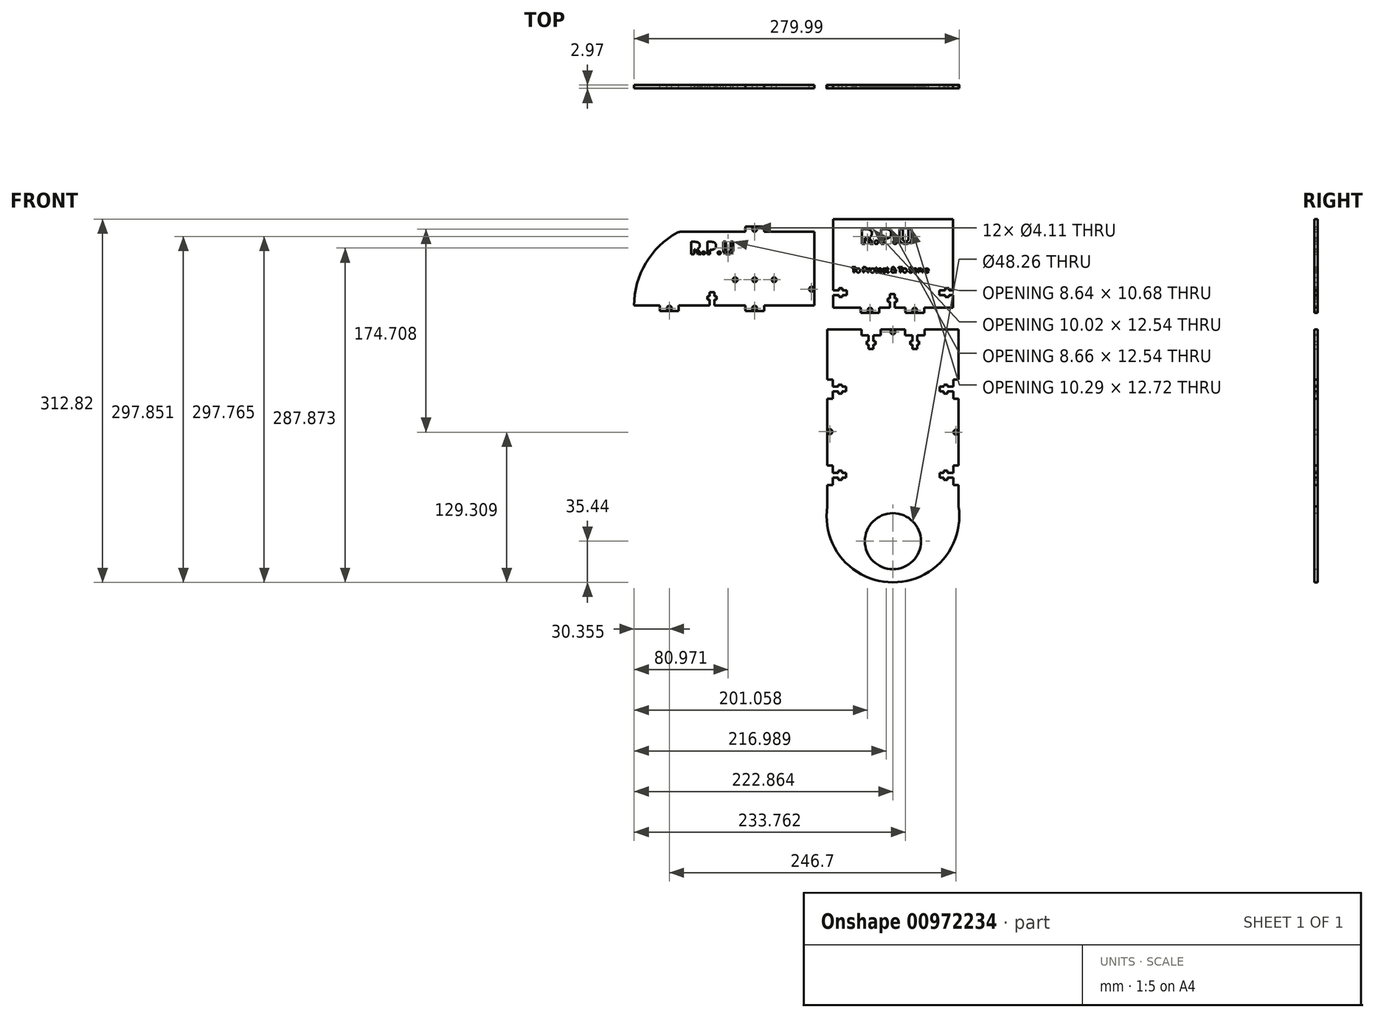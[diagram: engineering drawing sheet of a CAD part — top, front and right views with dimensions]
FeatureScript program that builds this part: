
annotation { "Feature Type Name" : "Feature", "Feature Type Description" : "" }
export const myFeature = defineFeature(function(context is Context, id is Id, definition is map)
    precondition{}
    {
        {
            var Q0;
            Q0=qCreatedBy(makeId("Front.planeOp"),FACE);
            var sketch = newSketch(context, id + "F0", { "sketchPlane" : qUnion([Q0])});
            skCircle(sketch, "E0", {"center": v(-10.51, -12.98) * mm, "radius": 2.06 * mm});
            skLineSegment(sketch, "E1.top", {"start": v(-18.6, -15.29) * mm, "end": v(-2.43, -15.29) * mm});
            skCircle(sketch, "E2", {"center": v(27.94, -12.98) * mm, "radius": 2.06 * mm});
            skLineSegment(sketch, "E3", {"start": v(19.85, -15.29) * mm, "end": v(36.02, -15.29) * mm});
            skLineSegment(sketch, "E4", {"start": v(-38.26, -10.74) * mm, "end": v(-18.6, -10.74) * mm});
            skLineSegment(sketch, "E5", {"start": v(-2.43, -15.29) * mm, "end": v(-2.43, -10.74) * mm});
            skLineSegment(sketch, "E6", {"start": v(-18.6, -15.29) * mm, "end": v(-18.6, -10.74) * mm});
            skLineSegment(sketch, "E7", {"start": v(36.02, -15.29) * mm, "end": v(36.02, -10.74) * mm});
            skLineSegment(sketch, "E8", {"start": v(19.85, -15.29) * mm, "end": v(19.85, -10.74) * mm});
            skLineSegment(sketch, "E9.trimOffspring", {"start": v(-2.43, -10.74) * mm, "end": v(6.65, -10.74) * mm});
            skLineSegment(sketch, "E10.trimOffspring", {"start": v(36.02, -10.74) * mm, "end": v(58.06, -10.74) * mm});
            skLineSegment(sketch, "E11", {"start": v(-38.26, -10.74) * mm, "end": v(-42.22, -10.74) * mm});
            skLineSegment(sketch, "E12", {"start": v(58.06, -10.74) * mm, "end": v(61.06, -10.74) * mm});
            skLineSegment(sketch, "E13", {"start": v(-42.22, 10.39) * mm, "end": v(-42.22, 4.11) * mm});
            skLineSegment(sketch, "E14", {"start": v(61.06, 10.39) * mm, "end": v(61.06, 4.11) * mm});
            skLineSegment(sketch, "E15", {"start": v(61.06, 0) * mm, "end": v(57.32, 0) * mm});
            skLineSegment(sketch, "E16.trimOffspring", {"start": v(61.06, 0) * mm, "end": v(61.06, -6.27) * mm});
            skLineSegment(sketch, "E17", {"start": v(-42.22, 0) * mm, "end": v(-37.14, 0) * mm});
            skLineSegment(sketch, "E18.trimOffspring", {"start": v(-42.22, 0) * mm, "end": v(-42.22, -6.27) * mm});
            skLineSegment(sketch, "E19", {"start": v(6.65, -10.74) * mm, "end": v(6.65, -5.66) * mm});
            skLineSegment(sketch, "E20.trimOffspring", {"start": v(10.77, -10.74) * mm, "end": v(19.85, -10.74) * mm});
            skLineSegment(sketch, "E21", {"start": v(-42.22, 65.46) * mm, "end": v(61.06, 65.46) * mm});
            skLineSegment(sketch, "E22.trimOffspring", {"start": v(-30.47, 4.11) * mm, "end": v(-34.21, 4.11) * mm});
            skLineSegment(sketch, "E23.trimOffspring", {"start": v(49.32, 4.11) * mm, "end": v(54.4, 4.11) * mm});
            skLineSegment(sketch, "E24.trimOffspring", {"start": v(10.77, 1) * mm, "end": v(10.77, -2.74) * mm});
            skText(sketch, "E25", { "text": "To Protect & To Serve", "fontName": "OpenSans-Bold.ttf"});
            skLineSegment(sketch, "E26", {"start": v(49.32, 4.11) * mm, "end": v(49.32, 0) * mm});
            skPoint(sketch, "E27.startSnap0", {"position": v(49.32, -3.14) * mm});
            skPoint(sketch, "E28.end.orphan", {"position": v(49.32, 10.39) * mm});
            skPoint(sketch, "E29.end.orphan", {"position": v(43.4, 10.39) * mm});
            skPoint(sketch, "E30.end.orphan", {"position": v(43.4, 4.11) * mm});
            skPoint(sketch, "E31.end.orphan", {"position": v(37.56, 4.11) * mm});
            skPoint(sketch, "E32.trimOffspring.end.orphan", {"position": v(37.56, 0) * mm});
            skPoint(sketch, "E33.end.orphan", {"position": v(43.4, 0) * mm});
            skPoint(sketch, "E34.end.orphan", {"position": v(43.4, -6.27) * mm});
            skPoint(sketch, "E35.orphan", {"position": v(49.32, -6.27) * mm});
            skLineSegment(sketch, "E36", {"start": v(54.4, -1.78) * mm, "end": v(57.32, -1.78) * mm});
            skLineSegment(sketch, "E37", {"start": v(57.32, -1.78) * mm, "end": v(57.32, 0) * mm});
            skLineSegment(sketch, "E38", {"start": v(54.4, 4.11) * mm, "end": v(54.4, 5.9) * mm});
            skLineSegment(sketch, "E39", {"start": v(54.4, 5.9) * mm, "end": v(57.3, 5.9) * mm});
            skLineSegment(sketch, "E40", {"start": v(57.3, 5.9) * mm, "end": v(57.3, 4.11) * mm});
            skLineSegment(sketch, "E41.trimOffspring", {"start": v(57.3, 4.11) * mm, "end": v(61.06, 4.11) * mm});
            skLineSegment(sketch, "E42", {"start": v(54.4, 0) * mm, "end": v(54.4, -1.78) * mm});
            skLineSegment(sketch, "E43.trimOffspring", {"start": v(54.4, 0) * mm, "end": v(49.32, 0) * mm});
            skLineSegment(sketch, "E44", {"start": v(-30.47, 4.11) * mm, "end": v(-30.47, 0) * mm});
            skLineSegment(sketch, "E45", {"start": v(6.65, 1) * mm, "end": v(10.77, 1) * mm});
            skLineSegment(sketch, "E46", {"start": v(61.06, -6.27) * mm, "end": v(61.06, -10.74) * mm});
            skPoint(sketch, "E47.orphan", {"position": v(65.6, -10.74) * mm});
            skPoint(sketch, "E48.start.orphan", {"position": v(65.6, -6.27) * mm});
            skLineSegment(sketch, "E49", {"start": v(-42.22, -6.27) * mm, "end": v(-42.22, -10.74) * mm});
            skPoint(sketch, "E50.orphan", {"position": v(-46.77, -10.74) * mm});
            skLineSegment(sketch, "E51", {"start": v(-37.14, 4.11) * mm, "end": v(-37.14, 5.9) * mm});
            skLineSegment(sketch, "E52", {"start": v(-37.14, 5.9) * mm, "end": v(-34.21, 5.9) * mm});
            skLineSegment(sketch, "E53", {"start": v(-34.21, 5.9) * mm, "end": v(-34.21, 4.11) * mm});
            skLineSegment(sketch, "E54.trimOffspring", {"start": v(-37.14, 4.11) * mm, "end": v(-42.22, 4.11) * mm});
            skLineSegment(sketch, "E55.trimOffspring", {"start": v(-34.21, 0) * mm, "end": v(-30.47, 0) * mm});
            skLineSegment(sketch, "E56", {"start": v(-37.14, 0) * mm, "end": v(-37.14, -1.75) * mm});
            skLineSegment(sketch, "E57", {"start": v(-37.14, -1.75) * mm, "end": v(-34.21, -1.75) * mm});
            skLineSegment(sketch, "E58", {"start": v(-34.21, -1.75) * mm, "end": v(-34.21, 0) * mm});
            skLineSegment(sketch, "E59", {"start": v(4.88, -5.66) * mm, "end": v(6.65, -5.66) * mm});
            skLineSegment(sketch, "E60", {"start": v(4.88, -5.66) * mm, "end": v(4.88, -2.74) * mm});
            skLineSegment(sketch, "E61", {"start": v(4.88, -2.74) * mm, "end": v(6.65, -2.74) * mm});
            skLineSegment(sketch, "E62", {"start": v(10.77, -5.66) * mm, "end": v(12.55, -5.66) * mm});
            skLineSegment(sketch, "E63", {"start": v(12.55, -5.66) * mm, "end": v(12.55, -2.74) * mm});
            skLineSegment(sketch, "E64", {"start": v(12.55, -2.74) * mm, "end": v(10.77, -2.74) * mm});
            skLineSegment(sketch, "E65.trimOffspring", {"start": v(10.77, -5.66) * mm, "end": v(10.77, -10.74) * mm});
            skLineSegment(sketch, "E66.trimOffspring", {"start": v(6.65, -2.74) * mm, "end": v(6.65, 1) * mm});
            skText(sketch, "E67", { "text": "R.P.U", "fontName": "OpenSans-Bold.ttf"});
            skLineSegment(sketch, "E68", {"start": v(-42.22, 10.39) * mm, "end": v(-42.22, 65.46) * mm});
            skPoint(sketch, "E69.orphan", {"position": v(-46.77, 65.46) * mm});
            skPoint(sketch, "E70.start.orphan", {"position": v(-46.77, 14.3) * mm});
            skLineSegment(sketch, "E71", {"start": v(61.06, 10.39) * mm, "end": v(61.06, 65.46) * mm});
            skPoint(sketch, "E72.end.orphan", {"position": v(65.6, 10.39) * mm});
            skPoint(sketch, "E72.start.orphan", {"position": v(65.6, 14.43) * mm});
            skPoint(sketch, "E73.orphan", {"position": v(65.6, 65.46) * mm});
            const initialGuessF0  = {"E25": [-0.02625, 0.0195, 1, 0, 0.00451], "E67": [-0.0192, 0.04422, 1, 0, 0.01265]};
            skSetInitialGuess(sketch, initialGuessF0);
            skSolve(sketch);
        }
        {
            var Q0;
            Q0=makeQuery(id+"F0.imprint","IMPRINT",FACE,{"disambiguationData":[TD([[makeQuery(id+"F0.imprint","IMPRINT",EDGE,{"derivedFrom":sQuery(id+"F0.wireOp",EDGE,"E0")}),-1.0]])]});
            extrude(context, id + "F1", {"entities" : qUnion([Q0]), "depth" : 2.97 * mm, "offsetDistance" : 25.4 * mm});
        }
        {
            var Q0;
            Q0=qCreatedBy(makeId("Front.planeOp"),FACE);
            var sketch = newSketch(context, id + "F2", { "sketchPlane" : qUnion([Q0])});
            skLineSegment(sketch, "E74", {"start": v(-36, -9.08) * mm, "end": v(-36, -2.95) * mm});
            skLineSegment(sketch, "E75", {"start": v(-36, -9.08) * mm, "end": v(-79.18, -9.08) * mm});
            skLineSegment(sketch, "E76", {"start": v(-79.18, -13.62) * mm, "end": v(-79.18, -9.08) * mm});
            skLineSegment(sketch, "E77", {"start": v(-79.18, -13.62) * mm, "end": v(-95.33, -13.62) * mm});
            skLineSegment(sketch, "E78", {"start": v(-95.33, -13.62) * mm, "end": v(-95.33, -9.08) * mm});
            skCircle(sketch, "E79", {"center": v(-87.25, -11.31) * mm, "radius": 2.06 * mm});
            skPoint(sketch, "E79.centerSnap0", {"position": v(-87.25, -13.62) * mm});
            skLineSegment(sketch, "E80.trimOffspring", {"start": v(-132.31, -9.08) * mm, "end": v(-152.63, -9.08) * mm});
            skLineSegment(sketch, "E81", {"start": v(-152.63, -13.62) * mm, "end": v(-152.63, -9.08) * mm});
            skLineSegment(sketch, "E82", {"start": v(-152.63, -13.62) * mm, "end": v(-168.79, -13.62) * mm});
            skLineSegment(sketch, "E83", {"start": v(-168.79, -13.62) * mm, "end": v(-168.79, -9.08) * mm});
            skCircle(sketch, "E84", {"center": v(-160.7, -11.31) * mm, "radius": 2.06 * mm});
            skPoint(sketch, "E84.centerSnap0", {"position": v(-160.7, -13.62) * mm});
            skLineSegment(sketch, "E85", {"start": v(-36, 54.42) * mm, "end": v(-79.18, 54.42) * mm});
            skLineSegment(sketch, "E86.trimOffspring", {"start": v(-95.33, -9.08) * mm, "end": v(-115.65, -9.08) * mm});
            skLineSegment(sketch, "E87.trimOffspring", {"start": v(-36, 13.2) * mm, "end": v(-36, 54.42) * mm});
            skLineSegment(sketch, "E88", {"start": v(-191.06, -9.08) * mm, "end": v(-168.79, -9.08) * mm});
            skLineSegment(sketch, "E89.trimOffspring", {"start": v(-168.79, 54.42) * mm, "end": v(-191.06, 54.42) * mm});
            skPoint(sketch, "E90", {"position": v(-87.25, 13.2) * mm});
            skCircle(sketch, "E91", {"center": v(-87.25, 13.2) * mm, "radius": 2.06 * mm});
            skCircle(sketch, "E92", {"center": v(-104.02, 13.2) * mm, "radius": 2.06 * mm});
            skCircle(sketch, "E93", {"center": v(-70.49, 13.2) * mm, "radius": 2.06 * mm});
            skText(sketch, "E94", { "text": "R.P.U\n", "fontName": "OpenSans-Bold.ttf"});
            skLineSegment(sketch, "E95", {"start": v(-191.06, 54.42) * mm, "end": v(-191.06, -9.08) * mm});
            skLineSegment(sketch, "E96", {"start": v(-168.79, 54.42) * mm, "end": v(-152.63, 54.42) * mm});
            skLineSegment(sketch, "E97", {"start": v(-95.33, 54.42) * mm, "end": v(-95.33, 58.97) * mm});
            skLineSegment(sketch, "E98", {"start": v(-95.33, 58.97) * mm, "end": v(-79.18, 58.97) * mm});
            skLineSegment(sketch, "E99", {"start": v(-79.18, 58.97) * mm, "end": v(-79.18, 54.42) * mm});
            skCircle(sketch, "E100", {"center": v(-87.25, 56.66) * mm, "radius": 2.06 * mm});
            skPoint(sketch, "E100.centerSnap0", {"position": v(-87.25, 58.97) * mm});
            skLineSegment(sketch, "E101.trimOffspring", {"start": v(-95.33, 54.42) * mm, "end": v(-152.63, 54.42) * mm});
            skArc(sketch, "E102", {"start": v(-152.63, 54.42) * mm, "mid": v(-180.7, 28.03) * mm, "end": v(-191.06, -9.08) * mm});
            skLineSegment(sketch, "E103", {"start": v(-36, 13.2) * mm, "end": v(-40.54, 13.2) * mm});
            skLineSegment(sketch, "E104", {"start": v(-36, -2.95) * mm, "end": v(-40.54, -2.95) * mm});
            skCircle(sketch, "E105", {"center": v(-38.3, 5.12) * mm, "radius": 2.06 * mm});
            skPoint(sketch, "E105.centerSnap0", {"position": v(-40.54, 5.12) * mm});
            skLineSegment(sketch, "E106", {"start": v(-36, 13.2) * mm, "end": v(-36, -2.95) * mm});
            skLineSegment(sketch, "E107", {"start": v(-132.31, -9.08) * mm, "end": v(-126.04, -9.08) * mm});
            skLineSegment(sketch, "E108", {"start": v(-115.65, -9.08) * mm, "end": v(-121.92, -9.08) * mm});
            skLineSegment(sketch, "E109", {"start": v(-121.92, -9.08) * mm, "end": v(-121.92, -4) * mm});
            skLineSegment(sketch, "E110", {"start": v(-126.04, -9.08) * mm, "end": v(-126.04, -4) * mm});
            skLineSegment(sketch, "E111", {"start": v(-126.04, -4) * mm, "end": v(-127.82, -4) * mm});
            skLineSegment(sketch, "E112", {"start": v(-127.82, -4) * mm, "end": v(-127.82, -1.08) * mm});
            skLineSegment(sketch, "E113", {"start": v(-127.82, -1.08) * mm, "end": v(-126.04, -1.08) * mm});
            skLineSegment(sketch, "E114", {"start": v(-121.92, -4) * mm, "end": v(-120.15, -4) * mm});
            skLineSegment(sketch, "E115", {"start": v(-120.15, -4) * mm, "end": v(-120.15, -1.08) * mm});
            skLineSegment(sketch, "E116", {"start": v(-120.15, -1.08) * mm, "end": v(-121.92, -1.08) * mm});
            skLineSegment(sketch, "E117", {"start": v(-121.92, -1.08) * mm, "end": v(-121.92, 2.66) * mm});
            skLineSegment(sketch, "E118", {"start": v(-126.04, -1.08) * mm, "end": v(-126.04, 2.66) * mm});
            skLineSegment(sketch, "E119", {"start": v(-126.04, 2.66) * mm, "end": v(-121.92, 2.66) * mm});
            const initialGuessF2  = {"E94": [-0.14308, 0.03532, 1, 0, 0.01062]};
            skSetInitialGuess(sketch, initialGuessF2);
            skSolve(sketch);
        }
        {
            var Q0;
            {var subQ1=sQuery(id+"F2.wireOp",EDGE,"OVJFDN25-UqmM-4DHd-mgfS-xPrGIr8piSGO");Q0=makeQuery(id+"F2.imprint","IMPRINT",FACE,{"disambiguationData":[TD([[makeQuery(id+"F2.imprint","IMPRINT",EDGE,{"derivedFrom":subQ1}),-1.0]])]});}
            var Q1;
            {var subQ2=sQuery(id+"F2.wireOp",EDGE,"OVJFDN25-UqmM-4DHd-mgfS-xPrGIr8piSGO");Q1=makeQuery(id+"F2.imprint","IMPRINT",FACE,{"disambiguationData":[TD([[makeQuery(id+"F2.imprint","IMPRINT",EDGE,{"derivedFrom":subQ2}),1.0]])]});}
            var Q2;
            {var subQ1=sQuery(id+"F2.wireOp",EDGE,"E76");Q2=makeQuery(id+"F2.imprint","IMPRINT",FACE,{"disambiguationData":[TD([[makeQuery(id+"F2.imprint","IMPRINT",EDGE,{"derivedFrom":subQ1}),1.0]])]});}
            extrude(context, id + "F3", {"entities" : qUnion([Q0, Q1, Q2]), "depth" : 2.97 * mm, "offsetDistance" : 25.4 * mm});
        }
        {
            var Q0;
            Q0=qCreatedBy(makeId("Front.planeOp"),FACE);
            var sketch = newSketch(context, id + "F4", { "sketchPlane" : qUnion([Q0])});
            skLineSegment(sketch, "E120", {"start": v(-47.3, -38.57) * mm, "end": v(-17.97, -38.57) * mm});
            skLineSegment(sketch, "E121", {"start": v(65.7, -38.57) * mm, "end": v(65.7, -81.75) * mm});
            skLineSegment(sketch, "E122", {"start": v(-47.3, -38.57) * mm, "end": v(-47.3, -81.75) * mm});
            skLineSegment(sketch, "E123", {"start": v(-47.3, -190.97) * mm, "end": v(65.7, -190.97) * mm});
            skLineSegment(sketch, "E124", {"start": v(65.7, -38.57) * mm, "end": v(36.36, -38.57) * mm});
            skLineSegment(sketch, "E125.trimOffspring", {"start": v(-1.3, -38.57) * mm, "end": v(19.7, -38.57) * mm});
            skCircle(sketch, "E126", {"center": v(9.2, -40.88) * mm, "radius": 2.06 * mm});
            skLineSegment(sketch, "E127", {"start": v(-17.97, -43.64) * mm, "end": v(-17.97, -38.57) * mm});
            skLineSegment(sketch, "E128", {"start": v(-17.97, -43.64) * mm, "end": v(-11.7, -43.64) * mm});
            skPoint(sketch, "E129.end.orphan", {"position": v(-8.78, -55.39) * mm});
            skLineSegment(sketch, "E130", {"start": v(-47.3, -81.75) * mm, "end": v(-42.74, -81.75) * mm});
            skLineSegment(sketch, "E131", {"start": v(-42.74, -98.41) * mm, "end": v(-47.3, -98.41) * mm});
            skLineSegment(sketch, "E132.trimOffspring", {"start": v(-47.3, -98.41) * mm, "end": v(-47.3, -119.12) * mm});
            skLineSegment(sketch, "E133", {"start": v(-42.74, -81.75) * mm, "end": v(-42.74, -88.02) * mm});
            skLineSegment(sketch, "E134", {"start": v(-42.74, -98.41) * mm, "end": v(-42.74, -92.14) * mm});
            skPoint(sketch, "E135.start.orphan", {"position": v(-42.74, -38.57) * mm});
            skPoint(sketch, "E136.start.orphan", {"position": v(-42.74, -118.73) * mm});
            skLineSegment(sketch, "E137.trimOffspring", {"start": v(-47.3, -135.27) * mm, "end": v(-47.3, -155.97) * mm});
            skLineSegment(sketch, "E138", {"start": v(-47.3, -155.97) * mm, "end": v(-42.74, -155.97) * mm});
            skLineSegment(sketch, "E139", {"start": v(-42.74, -172.63) * mm, "end": v(-47.3, -172.63) * mm});
            skLineSegment(sketch, "E140.trimOffspring", {"start": v(-47.3, -172.63) * mm, "end": v(-47.3, -190.97) * mm});
            skLineSegment(sketch, "E141", {"start": v(-42.74, -172.63) * mm, "end": v(-42.74, -166.36) * mm});
            skLineSegment(sketch, "E142", {"start": v(-42.74, -155.97) * mm, "end": v(-42.74, -162.24) * mm});
            skLineSegment(sketch, "E143", {"start": v(-42.74, -162.24) * mm, "end": v(-37.66, -162.24) * mm});
            skLineSegment(sketch, "E144", {"start": v(-42.74, -166.36) * mm, "end": v(-37.66, -166.36) * mm});
            skLineSegment(sketch, "E145", {"start": v(-42.74, -88.02) * mm, "end": v(-37.66, -88.02) * mm});
            skLineSegment(sketch, "E146", {"start": v(-42.74, -92.14) * mm, "end": v(-37.66, -92.14) * mm});
            skLineSegment(sketch, "E147", {"start": v(9.2, -40.88) * mm, "end": v(7.57, -38.57) * mm});
            skLineSegment(sketch, "E148", {"start": v(9.2, -40.88) * mm, "end": v(9.2, -190.97) * mm, "construction": true});
            skLineSegment(sketch, "E149.MirrorCS", {"start": v(65.7, -135.27) * mm, "end": v(65.7, -155.97) * mm});
            skLineSegment(sketch, "E150.MirrorCS", {"start": v(65.7, -172.63) * mm, "end": v(65.7, -190.97) * mm});
            skLineSegment(sketch, "E151.MirrorCS", {"start": v(65.7, -98.41) * mm, "end": v(65.7, -119.12) * mm});
            skPoint(sketch, "E152.MirrorP", {"position": v(61.12, -118.73) * mm});
            skLineSegment(sketch, "E153", {"start": v(-31, -92.14) * mm, "end": v(-31, -88.02) * mm});
            skLineSegment(sketch, "E154", {"start": v(-31, -162.24) * mm, "end": v(-31, -166.36) * mm});
            skPoint(sketch, "E155.start.orphan", {"position": v(-31, -155.6) * mm});
            skPoint(sketch, "E156.start.orphan", {"position": v(-31, -173.01) * mm});
            skPoint(sketch, "E157.end.orphan", {"position": v(-31, -98.03) * mm});
            skPoint(sketch, "E158.start.orphan", {"position": v(-25.08, -98.03) * mm});
            skPoint(sketch, "E159.start.orphan", {"position": v(-25.08, -92.14) * mm});
            skPoint(sketch, "E160.end.orphan", {"position": v(-19.24, -88.02) * mm});
            skPoint(sketch, "E160.start.orphan", {"position": v(-19.24, -91.37) * mm});
            skPoint(sketch, "E161.start.orphan", {"position": v(-31, -81.37) * mm});
            skPoint(sketch, "E162.end.orphan", {"position": v(-25.08, -88.02) * mm});
            skPoint(sketch, "E162.start.orphan", {"position": v(-25.08, -81.37) * mm});
            skPoint(sketch, "E163.end.orphan", {"position": v(-1.3, -61.3) * mm});
            skPoint(sketch, "E164.end.orphan", {"position": v(-4.55, -55.37) * mm});
            skPoint(sketch, "E165.end.orphan", {"position": v(-17.97, -55.37) * mm});
            skLineSegment(sketch, "E166", {"start": v(-37.66, -93.91) * mm, "end": v(-37.66, -92.14) * mm});
            skLineSegment(sketch, "E167", {"start": v(-37.66, -93.91) * mm, "end": v(-34.74, -93.91) * mm});
            skLineSegment(sketch, "E168", {"start": v(-34.74, -93.91) * mm, "end": v(-34.74, -92.14) * mm});
            skLineSegment(sketch, "E169", {"start": v(-37.66, -88.02) * mm, "end": v(-37.66, -86.24) * mm});
            skLineSegment(sketch, "E170", {"start": v(-37.66, -86.24) * mm, "end": v(-34.74, -86.24) * mm});
            skLineSegment(sketch, "E171", {"start": v(-34.74, -86.24) * mm, "end": v(-34.75, -88.02) * mm});
            skLineSegment(sketch, "E172.trimOffspring", {"start": v(-34.75, -88.02) * mm, "end": v(-31, -88.02) * mm});
            skLineSegment(sketch, "E173.trimOffspring", {"start": v(-34.74, -92.14) * mm, "end": v(-31, -92.14) * mm});
            skLineSegment(sketch, "E174", {"start": v(-37.66, -162.24) * mm, "end": v(-37.66, -160.47) * mm});
            skLineSegment(sketch, "E175", {"start": v(-37.66, -166.36) * mm, "end": v(-37.66, -168.13) * mm});
            skLineSegment(sketch, "E176", {"start": v(-37.66, -168.13) * mm, "end": v(-34.74, -168.13) * mm});
            skLineSegment(sketch, "E177", {"start": v(-34.74, -168.13) * mm, "end": v(-34.74, -166.36) * mm});
            skLineSegment(sketch, "E178", {"start": v(-37.66, -160.47) * mm, "end": v(-34.74, -160.47) * mm});
            skLineSegment(sketch, "E179", {"start": v(-34.74, -160.47) * mm, "end": v(-34.74, -162.24) * mm});
            skLineSegment(sketch, "E180.trimOffspring", {"start": v(-34.74, -162.24) * mm, "end": v(-31, -162.24) * mm});
            skLineSegment(sketch, "E181.trimOffspring", {"start": v(-34.74, -166.36) * mm, "end": v(-31, -166.36) * mm});
            skLineSegment(sketch, "E182", {"start": v(65.7, -135.27) * mm, "end": v(65.7, -135.44) * mm});
            skLineSegment(sketch, "E183.MirrorCS", {"start": v(53.13, -160.47) * mm, "end": v(53.13, -162.24) * mm});
            skLineSegment(sketch, "E184.MirrorCS", {"start": v(56.05, -88.02) * mm, "end": v(56.05, -86.24) * mm});
            skLineSegment(sketch, "E185.MirrorCS", {"start": v(56.05, -86.24) * mm, "end": v(53.13, -86.24) * mm});
            skLineSegment(sketch, "E186.MirrorCS", {"start": v(53.13, -86.24) * mm, "end": v(53.14, -88.02) * mm});
            skLineSegment(sketch, "E187.MirrorCS", {"start": v(53.13, -93.91) * mm, "end": v(53.13, -92.14) * mm});
            skLineSegment(sketch, "E188.MirrorCS", {"start": v(56.05, -93.91) * mm, "end": v(56.05, -92.14) * mm});
            skLineSegment(sketch, "E189.MirrorCS", {"start": v(61.12, -166.36) * mm, "end": v(56.05, -166.36) * mm});
            skLineSegment(sketch, "E190.MirrorCS", {"start": v(56.05, -93.91) * mm, "end": v(53.13, -93.91) * mm});
            skLineSegment(sketch, "E191.MirrorCS", {"start": v(53.13, -92.14) * mm, "end": v(49.39, -92.14) * mm});
            skLineSegment(sketch, "E192.MirrorCS", {"start": v(56.05, -160.47) * mm, "end": v(53.13, -160.47) * mm});
            skLineSegment(sketch, "E193.MirrorCS", {"start": v(53.13, -162.24) * mm, "end": v(49.39, -162.24) * mm});
            skLineSegment(sketch, "E194.MirrorCS", {"start": v(56.05, -162.24) * mm, "end": v(56.05, -160.47) * mm});
            skLineSegment(sketch, "E195.MirrorCS", {"start": v(49.39, -162.24) * mm, "end": v(49.39, -166.36) * mm});
            skLineSegment(sketch, "E196.MirrorCS", {"start": v(53.14, -88.02) * mm, "end": v(49.39, -88.02) * mm});
            skLineSegment(sketch, "E197.MirrorCS", {"start": v(49.39, -92.14) * mm, "end": v(49.39, -88.02) * mm});
            skLineSegment(sketch, "E198.MirrorCS", {"start": v(61.12, -88.02) * mm, "end": v(56.05, -88.02) * mm});
            skLineSegment(sketch, "E199.MirrorCS", {"start": v(56.05, -168.13) * mm, "end": v(53.13, -168.13) * mm});
            skLineSegment(sketch, "E200.MirrorCS", {"start": v(56.05, -166.36) * mm, "end": v(56.05, -168.13) * mm});
            skLineSegment(sketch, "E201.MirrorCS", {"start": v(53.13, -168.13) * mm, "end": v(53.13, -166.36) * mm});
            skLineSegment(sketch, "E202.MirrorCS", {"start": v(53.13, -166.36) * mm, "end": v(49.39, -166.36) * mm});
            skLineSegment(sketch, "E203.MirrorCS", {"start": v(61.12, -92.14) * mm, "end": v(56.05, -92.14) * mm});
            skLineSegment(sketch, "E204.MirrorCS", {"start": v(61.12, -172.63) * mm, "end": v(61.12, -166.36) * mm});
            skLineSegment(sketch, "E205.MirrorCS", {"start": v(61.12, -162.24) * mm, "end": v(56.05, -162.24) * mm});
            skLineSegment(sketch, "E206.MirrorCS", {"start": v(61.12, -81.75) * mm, "end": v(61.12, -88.02) * mm});
            skLineSegment(sketch, "E207.MirrorCS", {"start": v(61.12, -98.41) * mm, "end": v(61.12, -92.14) * mm});
            skLineSegment(sketch, "E208.MirrorCS", {"start": v(61.12, -98.41) * mm, "end": v(65.7, -98.41) * mm});
            skLineSegment(sketch, "E209.MirrorCS", {"start": v(61.12, -155.97) * mm, "end": v(61.12, -162.24) * mm});
            skLineSegment(sketch, "E210.MirrorCS", {"start": v(65.7, -155.97) * mm, "end": v(61.12, -155.97) * mm});
            skLineSegment(sketch, "E211.MirrorCS", {"start": v(65.7, -81.75) * mm, "end": v(61.12, -81.75) * mm});
            skLineSegment(sketch, "E212.MirrorCS", {"start": v(61.12, -172.63) * mm, "end": v(65.7, -172.63) * mm});
            skPoint(sketch, "E213.MirrorP", {"position": v(49.39, -155.6) * mm});
            skPoint(sketch, "E214.MirrorP", {"position": v(43.47, -88.02) * mm});
            skLineSegment(sketch, "E215.MirrorCS", {"start": v(19.7, -38.57) * mm, "end": v(-1.3, -38.57) * mm});
            skPoint(sketch, "E216.MirrorP", {"position": v(43.47, -81.37) * mm});
            skPoint(sketch, "E217.MirrorP", {"position": v(49.39, -81.37) * mm});
            skPoint(sketch, "E218.MirrorP", {"position": v(61.12, -38.57) * mm});
            skPoint(sketch, "E219.MirrorP", {"position": v(37.63, -88.02) * mm});
            skPoint(sketch, "E220.MirrorP", {"position": v(43.47, -92.14) * mm});
            skPoint(sketch, "E221.MirrorP", {"position": v(37.63, -91.37) * mm});
            skPoint(sketch, "E222.MirrorP", {"position": v(49.39, -173.01) * mm});
            skPoint(sketch, "E223.MirrorP", {"position": v(49.39, -98.03) * mm});
            skPoint(sketch, "E224.MirrorP", {"position": v(43.47, -98.03) * mm});
            skArc(sketch, "E225", {"start": v(-47.3, -190.97) * mm, "mid": v(9.2, -256.5) * mm, "end": v(65.7, -190.97) * mm});
            skCircle(sketch, "E226", {"center": v(9.2, -221.06) * mm, "radius": 24.13 * mm});
            skLineSegment(sketch, "E227", {"start": v(65.7, -119.12) * mm, "end": v(61.12, -119.12) * mm});
            skLineSegment(sketch, "E228", {"start": v(65.7, -135.27) * mm, "end": v(61.12, -135.27) * mm});
            skLineSegment(sketch, "E229", {"start": v(65.7, -119.12) * mm, "end": v(65.7, -135.27) * mm});
            skCircle(sketch, "E230", {"center": v(63.38, -127.2) * mm, "radius": 2.06 * mm});
            skPoint(sketch, "E230.centerSnap0", {"position": v(61.12, -127.2) * mm});
            skLineSegment(sketch, "E231", {"start": v(-47.3, -135.27) * mm, "end": v(-42.74, -135.27) * mm});
            skLineSegment(sketch, "E232", {"start": v(-42.74, -119.12) * mm, "end": v(-47.3, -119.12) * mm});
            skLineSegment(sketch, "E233", {"start": v(-47.3, -119.12) * mm, "end": v(-47.3, -135.27) * mm});
            skCircle(sketch, "E234", {"center": v(-45, -126.77) * mm, "radius": 2.06 * mm});
            skLineSegment(sketch, "E235.trimOffspring", {"start": v(36.36, -38.57) * mm, "end": v(65.7, -38.57) * mm});
            skPoint(sketch, "E236.trimOffspring.end.orphan", {"position": v(35.47, -38.57) * mm});
            skPoint(sketch, "E236.trimOffspring.start.orphan", {"position": v(36.36, -38.57) * mm});
            skLineSegment(sketch, "E237", {"start": v(-1.3, -38.57) * mm, "end": v(-1.3, -43.64) * mm});
            skLineSegment(sketch, "E238", {"start": v(-1.3, -43.64) * mm, "end": v(-7.58, -43.64) * mm});
            skLineSegment(sketch, "E239", {"start": v(-7.58, -43.64) * mm, "end": v(-7.58, -48.72) * mm});
            skLineSegment(sketch, "E240", {"start": v(-7.58, -48.72) * mm, "end": v(-5.8, -48.72) * mm});
            skLineSegment(sketch, "E241", {"start": v(-5.8, -48.72) * mm, "end": v(-5.8, -51.64) * mm});
            skLineSegment(sketch, "E242", {"start": v(-5.8, -51.64) * mm, "end": v(-7.58, -51.64) * mm});
            skLineSegment(sketch, "E243", {"start": v(-7.58, -51.64) * mm, "end": v(-7.58, -55.39) * mm});
            skLineSegment(sketch, "E244", {"start": v(-11.7, -43.64) * mm, "end": v(-11.7, -48.72) * mm});
            skLineSegment(sketch, "E245", {"start": v(-11.7, -48.72) * mm, "end": v(-13.48, -48.72) * mm});
            skLineSegment(sketch, "E246", {"start": v(-13.48, -48.72) * mm, "end": v(-13.48, -51.64) * mm});
            skLineSegment(sketch, "E247", {"start": v(-13.48, -51.64) * mm, "end": v(-11.7, -51.64) * mm});
            skLineSegment(sketch, "E248", {"start": v(-11.7, -51.64) * mm, "end": v(-11.7, -55.39) * mm});
            skLineSegment(sketch, "E249", {"start": v(-11.7, -55.39) * mm, "end": v(-7.58, -55.39) * mm});
            skLineSegment(sketch, "E250", {"start": v(35.47, -38.57) * mm, "end": v(36.36, -38.57) * mm});
            skLineSegment(sketch, "E251.MirrorCS", {"start": v(36.36, -43.64) * mm, "end": v(36.36, -38.57) * mm});
            skLineSegment(sketch, "E252.MirrorCS", {"start": v(36.36, -43.64) * mm, "end": v(30.09, -43.64) * mm});
            skLineSegment(sketch, "E253.MirrorCS", {"start": v(31.86, -51.64) * mm, "end": v(30.09, -51.64) * mm});
            skLineSegment(sketch, "E254.MirrorCS", {"start": v(25.97, -48.72) * mm, "end": v(24.2, -48.72) * mm});
            skLineSegment(sketch, "E255.MirrorCS", {"start": v(30.09, -48.72) * mm, "end": v(31.86, -48.72) * mm});
            skLineSegment(sketch, "E256.MirrorCS", {"start": v(24.2, -51.64) * mm, "end": v(25.97, -51.64) * mm});
            skLineSegment(sketch, "E257.MirrorCS", {"start": v(24.2, -48.72) * mm, "end": v(24.2, -51.64) * mm});
            skLineSegment(sketch, "E258.MirrorCS", {"start": v(19.7, -43.64) * mm, "end": v(25.97, -43.64) * mm});
            skPoint(sketch, "E259.MirrorP", {"position": v(22.94, -55.37) * mm});
            skLineSegment(sketch, "E260.MirrorCS", {"start": v(30.09, -51.64) * mm, "end": v(30.09, -55.39) * mm});
            skLineSegment(sketch, "E261.MirrorCS", {"start": v(30.09, -55.39) * mm, "end": v(25.97, -55.39) * mm});
            skPoint(sketch, "E262.MirrorP", {"position": v(27.17, -55.39) * mm});
            skLineSegment(sketch, "E263.MirrorCS", {"start": v(31.86, -48.72) * mm, "end": v(31.86, -51.64) * mm});
            skLineSegment(sketch, "E264.MirrorCS", {"start": v(19.7, -38.57) * mm, "end": v(19.7, -43.64) * mm});
            skLineSegment(sketch, "E265.MirrorCS", {"start": v(25.97, -43.64) * mm, "end": v(25.97, -48.72) * mm});
            skLineSegment(sketch, "E266.MirrorCS", {"start": v(30.09, -43.64) * mm, "end": v(30.09, -48.72) * mm});
            skLineSegment(sketch, "E267.MirrorCS", {"start": v(25.97, -51.64) * mm, "end": v(25.97, -55.39) * mm});
            skSolve(sketch);
        }
        {
            var Q0;
            Q0=makeQuery(id+"F4.imprint","IMPRINT",FACE,{"disambiguationData":[TD([[makeQuery(id+"F4.imprint","IMPRINT",EDGE,{"derivedFrom":sQuery(id+"F4.wireOp",EDGE,"E120")}),-1.0]])]});
            var Q1;
            Q1=makeQuery(id+"F4.imprint","IMPRINT",FACE,{"disambiguationData":[TD([[makeQuery(id+"F4.imprint","IMPRINT",EDGE,{"derivedFrom":sQuery(id+"F4.wireOp",EDGE,"E123")}),-1.0]])]});
            extrude(context, id + "F5", {"entities" : qUnion([Q0, Q1]), "depth" : 2.97 * mm, "offsetDistance" : 25.4 * mm});
        }
        {
            var Q0;
            Q0=makeQuery(id+"F3.opExtrude","SWEPT_BODY",BODY,{"disambiguationData":[OSD([sQuery(id+"F2.wireOp",EDGE,"E74"),sQuery(id+"F2.wireOp",EDGE,"h8QSBksQ-YwWN-TbQ9-orer-dnY7yjln7PkG"),sQuery(id+"F2.wireOp",EDGE,"uAboEah3-f3y6-R4XF-ticJ-74GYFwzw9mUI"),sQuery(id+"F2.wireOp",EDGE,"ObChG0I8-zuCY-XqXA-1VoJ-OzmpDoP1xZaO"),sQuery(id+"F2.wireOp",EDGE,"RWAwpEoa-BUGJ-aAW7-ngYd-DeukXgGkUtki"),sQuery(id+"F2.wireOp",EDGE,"E75"),sQuery(id+"F2.wireOp",EDGE,"E76"),sQuery(id+"F2.wireOp",EDGE,"E77"),sQuery(id+"F2.wireOp",EDGE,"E78"),sQuery(id+"F2.wireOp",EDGE,"E79"),sQuery(id+"F2.wireOp",EDGE,"FA6daFXN-mA14-maJo-ga2L-fxs06plftmtT"),sQuery(id+"F2.wireOp",EDGE,"6SFBSKkV-7Q2o-Axrq-HpiS-Oonq6Mo3bD0O"),sQuery(id+"F2.wireOp",EDGE,"smFho10Q-fqs9-7RC2-xNXY-59qUfedKx50k"),sQuery(id+"F2.wireOp",EDGE,"0RSeY66L-Zm8g-s7ti-8wWv-ubc7zTPof324"),sQuery(id+"F2.wireOp",EDGE,"E80.trimOffspring"),sQuery(id+"F2.wireOp",EDGE,"rjME6JAt-dFvn-6o0u-LxmC-vMUpvvn9hbSr"),sQuery(id+"F2.wireOp",EDGE,"ADrRUh6O-BrmG-nYIV-0qPf-Y4BKHcjhDC0A"),sQuery(id+"F2.wireOp",EDGE,"3TV9EzE3-sWAf-CArM-Ep5Z-BIaoFF90LYxw"),sQuery(id+"F2.wireOp",EDGE,"a68d64ff-956a-435a-b33e-cca1a7969c3b.trimOffspring"),sQuery(id+"F2.wireOp",EDGE,"5fb2db7f-7043-40fa-93e5-e43134f58009.trimOffspring"),sQuery(id+"F2.wireOp",EDGE,"E81"),sQuery(id+"F2.wireOp",EDGE,"E82"),sQuery(id+"F2.wireOp",EDGE,"E83"),sQuery(id+"F2.wireOp",EDGE,"E84"),sQuery(id+"F2.wireOp",EDGE,"E85"),sQuery(id+"F2.wireOp",EDGE,"Pv8xFsH5-YH5J-F9ey-8Fvg-MMiklTOo1uKY"),sQuery(id+"F2.wireOp",EDGE,"U4XKn8nQ-U5P0-jo1P-f3DY-XsQpFrBLSVEV"),sQuery(id+"F2.wireOp",EDGE,"E86.trimOffspring"),sQuery(id+"F2.wireOp",EDGE,"E87.trimOffspring"),sQuery(id+"F2.wireOp",EDGE,"E88"),sQuery(id+"F2.wireOp",EDGE,"mWaTCWFI-yoWM-3zpX-jkwn-Rgp68r4fxPfJ"),sQuery(id+"F2.wireOp",EDGE,"91H7TU5L-Fhsu-F0zj-jWK8-o2j0VNuX0pwp"),sQuery(id+"F2.wireOp",EDGE,"qoczEJfj-F8Mu-Nipv-6qPa-pGaxWbRDdk7T"),sQuery(id+"F2.wireOp",EDGE,"wubdM6Ff-gfYk-hoTW-XXbH-Zjq5QOPTjgNT"),sQuery(id+"F2.wireOp",EDGE,"HgigmK6g-IEM9-Paxe-Iuo1-wTw0BSureikm"),sQuery(id+"F2.wireOp",EDGE,"6HSvZUGX-GTlK-ZPIf-wiT4-QNAPdHBzlkyh")])]});
            transform(context, id + "F6", {"entities" : qUnion([Q0]), "transformType" : TransformType.TRANSLATION_3D, "dx" : -22.6 * mm, "dy" : 0 * mm, "dz" : 0 * mm, "makeCopy" : false});
        }
        {
            var Q0;
            Q0=makeQuery(id+"F5.opExtrude","SWEPT_BODY",BODY,{"disambiguationData":[OSD([sQuery(id+"F4.wireOp",EDGE,"E120"),sQuery(id+"F4.wireOp",EDGE,"E122"),sQuery(id+"F4.wireOp",EDGE,"E123"),sQuery(id+"F4.wireOp",EDGE,"iohXHTiQ-WZw0-uzqA-dxWK-AKoeT3LojtUM"),sQuery(id+"F4.wireOp",EDGE,"vfdezHYI-Djgr-QXE8-sTUR-rBvkQ3WOczKf"),sQuery(id+"F4.wireOp",EDGE,"W6a4G9Vi-0zfl-fg3l-nADc-uZA2LnvQPdxn"),sQuery(id+"F4.wireOp",EDGE,"E125.trimOffspring"),sQuery(id+"F4.wireOp",EDGE,"728db415-b518-4be5-a76a-9e382e2fbad3.trimOffspring"),sQuery(id+"F4.wireOp",EDGE,"E126"),sQuery(id+"F4.wireOp",EDGE,"E127"),sQuery(id+"F4.wireOp",EDGE,"fBH0bQyB-7pDb-zp6R-fFLW-huZ92iLANuKE"),sQuery(id+"F4.wireOp",EDGE,"AZO88fip-mGbl-6Dei-PWM3-G2eas2MXL09o"),sQuery(id+"F4.wireOp",EDGE,"E128"),sQuery(id+"F4.wireOp",EDGE,"433b67b9-89b6-4bd4-9f6b-d9995bbf40bb.trimOffspring"),sQuery(id+"F4.wireOp",EDGE,"djrUTvu5-jOnd-LCKp-OXDw-zwsYnCnUUO5E"),sQuery(id+"F4.wireOp",EDGE,"jN90LYXF-18CP-ewbM-9wpE-UafqxCrIqDik"),sQuery(id+"F4.wireOp",EDGE,"MPhkbVXa-Q5H0-YIBG-w0Uo-dK8bkDSnbjNX"),sQuery(id+"F4.wireOp",EDGE,"E165"),sQuery(id+"F4.wireOp",EDGE,"E164"),sQuery(id+"F4.wireOp",EDGE,"E163"),sQuery(id+"F4.wireOp",EDGE,"Z9JU0RtP-j2Ds-im0Y-uYlW-AMYMXmYoOT2z"),sQuery(id+"F4.wireOp",EDGE,"IsXDuKsY-V33o-LbIT-R2wh-dUf2o97h5ovw"),sQuery(id+"F4.wireOp",EDGE,"kVo7Gtra-9okj-y65i-vAf9-WddWx6PrIhSH"),sQuery(id+"F4.wireOp",EDGE,"avL2HHKr-m1AU-U303-Gx2r-zEUsVELeELSp"),sQuery(id+"F4.wireOp",EDGE,"Iia4y8p5-lMCh-cjUo-4Gru-s2HIaUgALJqL"),sQuery(id+"F4.wireOp",EDGE,"dkRDQeNF-bp09-174G-H3ED-4MkwwZmdMrWS"),sQuery(id+"F4.wireOp",EDGE,"IA7QH3u4-Lbta-FUUF-51SA-xqP7VuBKAvmc"),sQuery(id+"F4.wireOp",EDGE,"VlRwcdI5-8AQM-u4kQ-HBDJ-s0uAhNUMzu6l"),sQuery(id+"F4.wireOp",EDGE,"ICQ3ALdX-dZFh-yGKg-883H-VfHNaUW2OBmi"),sQuery(id+"F4.wireOp",EDGE,"09z2Ze5b-oeJ5-MJT1-rL1R-CWUheOGahaKp"),sQuery(id+"F4.wireOp",EDGE,"kIqyvfzb-Tb18-RJTh-MImL-BTeGV0cvtQuR"),sQuery(id+"F4.wireOp",EDGE,"YpEDKD9l-hypC-jMpX-Njah-JU3KhnVQk5uF"),sQuery(id+"F4.wireOp",EDGE,"zmrpWeGd-UjRu-5kt0-ckeH-GbkOG4DqARqv"),sQuery(id+"F4.wireOp",EDGE,"wBeqmctE-u76Y-yKJe-hdrd-yoPC8vgtup2Y"),sQuery(id+"F4.wireOp",EDGE,"E130"),sQuery(id+"F4.wireOp",EDGE,"E131"),sQuery(id+"F4.wireOp",EDGE,"E132.trimOffspring"),sQuery(id+"F4.wireOp",EDGE,"E133"),sQuery(id+"F4.wireOp",EDGE,"E134"),sQuery(id+"F4.wireOp",EDGE,"AfFT5X04-QW7y-rJ40-yOIU-52HpOTHjm1kR"),sQuery(id+"F4.wireOp",EDGE,"QF4YAIKC-nRPv-IMqE-LyZK-v6vDkGEZSOWo"),sQuery(id+"F4.wireOp",EDGE,"eonl8MaW-ZRqC-m8H9-ZJAa-lOhg9YHUABmc"),sQuery(id+"F4.wireOp",EDGE,"E137.trimOffspring"),sQuery(id+"F4.wireOp",EDGE,"01QxeS0O-2dLb-vxbK-YPBv-Q9qslvDmqtue"),sQuery(id+"F4.wireOp",EDGE,"E160"),sQuery(id+"F4.wireOp",EDGE,"E138"),sQuery(id+"F4.wireOp",EDGE,"E139"),sQuery(id+"F4.wireOp",EDGE,"E140.trimOffspring"),sQuery(id+"F4.wireOp",EDGE,"E141"),sQuery(id+"F4.wireOp",EDGE,"E142"),sQuery(id+"F4.wireOp",EDGE,"I5dM6OyK-C2i5-N1ZM-TPve-bCS8jZquYYvb"),sQuery(id+"F4.wireOp",EDGE,"E143"),sQuery(id+"F4.wireOp",EDGE,"E144"),sQuery(id+"F4.wireOp",EDGE,"EQ092Qmf-d7RL-dsFj-pDk6-DLwWH4ga1MS3"),sQuery(id+"F4.wireOp",EDGE,"v4hw12ON-Kn0A-zcPN-AWdy-wjujSs07YwIl"),sQuery(id+"F4.wireOp",EDGE,"E155"),sQuery(id+"F4.wireOp",EDGE,"E156"),sQuery(id+"F4.wireOp",EDGE,"zHJcAi4G-vBjZ-PVc6-LSNt-6IGNiOixcgHz"),sQuery(id+"F4.wireOp",EDGE,"2icb326b-f8xt-jkox-nxTX-71DODKz5sswn"),sQuery(id+"F4.wireOp",EDGE,"DX3dQZYj-01vy-VJUN-FvUS-dIxg25u6yKv1"),sQuery(id+"F4.wireOp",EDGE,"vxZwufvW-1V3q-RiER-lRlK-IPzvBX9lEgKX"),sQuery(id+"F4.wireOp",EDGE,"E145"),sQuery(id+"F4.wireOp",EDGE,"E146"),sQuery(id+"F4.wireOp",EDGE,"Qwjh03jz-hG1A-jDlJ-MnOI-GFsmHNh0qciF"),sQuery(id+"F4.wireOp",EDGE,"E157"),sQuery(id+"F4.wireOp",EDGE,"E161"),sQuery(id+"F4.wireOp",EDGE,"TUlHPbTQ-i3I6-dmwq-wYJE-hk0mlEAQnZBi"),sQuery(id+"F4.wireOp",EDGE,"E158"),sQuery(id+"F4.wireOp",EDGE,"E159"),sQuery(id+"F4.wireOp",EDGE,"tHNRsyOz-VRlC-hlZC-n81j-1N2cYH4iIsKC"),sQuery(id+"F4.wireOp",EDGE,"E162"),sQuery(id+"F4.wireOp",EDGE,"46cc8c59-18d4-4094-b739-0333371662790.MirrorCS"),sQuery(id+"F4.wireOp",EDGE,"E121"),sQuery(id+"F4.wireOp",EDGE,"46cc8c59-18d4-4094-b739-0333371662792.MirrorCS"),sQuery(id+"F4.wireOp",EDGE,"46cc8c59-18d4-4094-b739-0333371662793.MirrorCS"),sQuery(id+"F4.wireOp",EDGE,"46cc8c59-18d4-4094-b739-0333371662794.MirrorCS"),sQuery(id+"F4.wireOp",EDGE,"46cc8c59-18d4-4094-b739-0333371662795.MirrorCS"),sQuery(id+"F4.wireOp",EDGE,"46cc8c59-18d4-4094-b739-0333371662796.MirrorCS"),sQuery(id+"F4.wireOp",EDGE,"46cc8c59-18d4-4094-b739-0333371662797.MirrorCS"),sQuery(id+"F4.wireOp",EDGE,"46cc8c59-18d4-4094-b739-0333371662798.MirrorCS"),sQuery(id+"F4.wireOp",EDGE,"46cc8c59-18d4-4094-b739-0333371662799.MirrorCS"),sQuery(id+"F4.wireOp",EDGE,"46cc8c59-18d4-4094-b739-03333716627910.MirrorCS"),sQuery(id+"F4.wireOp",EDGE,"46cc8c59-18d4-4094-b739-03333716627911.MirrorCS"),sQuery(id+"F4.wireOp",EDGE,"46cc8c59-18d4-4094-b739-03333716627912.MirrorCS"),sQuery(id+"F4.wireOp",EDGE,"46cc8c59-18d4-4094-b739-03333716627913.MirrorCS"),sQuery(id+"F4.wireOp",EDGE,"46cc8c59-18d4-4094-b739-03333716627914.MirrorCS"),sQuery(id+"F4.wireOp",EDGE,"46cc8c59-18d4-4094-b739-03333716627915.MirrorCS"),sQuery(id+"F4.wireOp",EDGE,"46cc8c59-18d4-4094-b739-03333716627916.MirrorCS"),sQuery(id+"F4.wireOp",EDGE,"46cc8c59-18d4-4094-b739-03333716627917.MirrorCS"),sQuery(id+"F4.wireOp",EDGE,"46cc8c59-18d4-4094-b739-03333716627918.MirrorCS"),sQuery(id+"F4.wireOp",EDGE,"46cc8c59-18d4-4094-b739-03333716627919.MirrorCS"),sQuery(id+"F4.wireOp",EDGE,"46cc8c59-18d4-4094-b739-03333716627920.MirrorCS"),sQuery(id+"F4.wireOp",EDGE,"46cc8c59-18d4-4094-b739-03333716627921.MirrorCS"),sQuery(id+"F4.wireOp",EDGE,"46cc8c59-18d4-4094-b739-03333716627922.MirrorCS"),sQuery(id+"F4.wireOp",EDGE,"46cc8c59-18d4-4094-b739-03333716627923.MirrorCS"),sQuery(id+"F4.wireOp",EDGE,"46cc8c59-18d4-4094-b739-03333716627924.MirrorCS"),sQuery(id+"F4.wireOp",EDGE,"46cc8c59-18d4-4094-b739-03333716627925.MirrorCS"),sQuery(id+"F4.wireOp",EDGE,"46cc8c59-18d4-4094-b739-03333716627926.MirrorCS"),sQuery(id+"F4.wireOp",EDGE,"46cc8c59-18d4-4094-b739-03333716627927.MirrorCS"),sQuery(id+"F4.wireOp",EDGE,"46cc8c59-18d4-4094-b739-03333716627928.MirrorCS"),sQuery(id+"F4.wireOp",EDGE,"46cc8c59-18d4-4094-b739-03333716627929.MirrorCS"),sQuery(id+"F4.wireOp",EDGE,"46cc8c59-18d4-4094-b739-03333716627930.MirrorCS"),sQuery(id+"F4.wireOp",EDGE,"46cc8c59-18d4-4094-b739-03333716627931.MirrorCS"),sQuery(id+"F4.wireOp",EDGE,"46cc8c59-18d4-4094-b739-03333716627932.MirrorCS"),sQuery(id+"F4.wireOp",EDGE,"46cc8c59-18d4-4094-b739-03333716627933.MirrorCS"),sQuery(id+"F4.wireOp",EDGE,"46cc8c59-18d4-4094-b739-03333716627937.MirrorC"),sQuery(id+"F4.wireOp",EDGE,"E151.MirrorCS"),sQuery(id+"F4.wireOp",EDGE,"E149.MirrorCS"),sQuery(id+"F4.wireOp",EDGE,"E150.MirrorCS"),sQuery(id+"F4.wireOp",EDGE,"VkYVsUMz-jEfg-iXTA-U9YV-3PSOp7gkSMdf"),sQuery(id+"F4.wireOp",EDGE,"9gqKMNus-jgme-gqoE-X7sW-LnfjHIVMowt6")])]});
            transform(context, id + "F7", {"entities" : qUnion([Q0]), "transformType" : TransformType.TRANSLATION_3D, "dx" : 0 * mm, "dy" : 0 * mm, "dz" : 9.14 * mm, "makeCopy" : false});
        }
        {
            var Q0;
            Q0=makeQuery(id+"F3.opExtrude","SWEPT_EDGE",EDGE,{"disambiguationData":[OSD([sQuery(id+"F2.wireOp",EDGE,"E96"),sQuery(id+"F2.wireOp",EDGE,"E101.trimOffspring"),sQuery(id+"F2.wireOp",EDGE,"E102")])]});
            fillet(context, id + "F8", {"entities" : qUnion([Q0]), "radius" : 5.08 * mm, "tangentPropagation" : true, "allowEdgeOverflow" : false});
        }
    });
